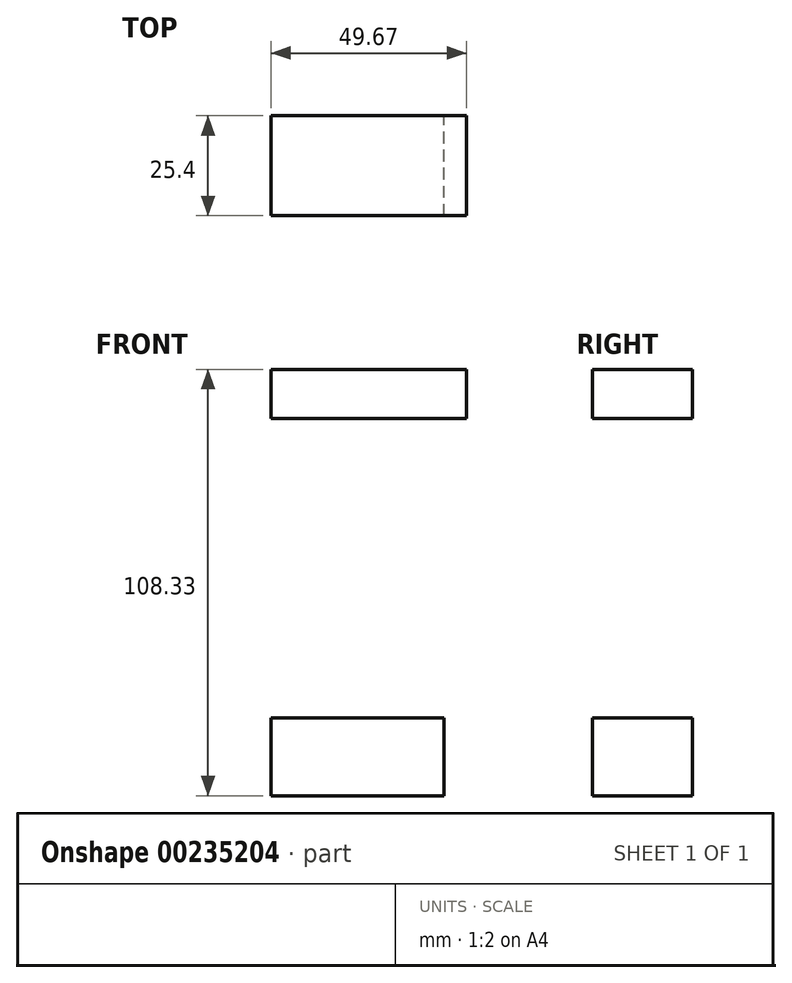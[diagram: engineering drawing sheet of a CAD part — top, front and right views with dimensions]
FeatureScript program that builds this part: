
annotation { "Feature Type Name" : "Feature", "Feature Type Description" : "" }
export const myFeature = defineFeature(function(context is Context, id is Id, definition is map)
    precondition{}
    {
        {
            var Q0;
            Q0=qCreatedBy(makeId("Front.planeOp"),FACE);
            var sketch = newSketch(context, id + "F0", { "sketchPlane" : qUnion([Q0])});
            skLineSegment(sketch, "E0.bottom", {"start": v(49.67, 35.29) * mm, "end": v(0, 35.29) * mm});
            skLineSegment(sketch, "E0.top", {"start": v(49.67, 47.75) * mm, "end": v(0, 47.75) * mm});
            skLineSegment(sketch, "E0.left", {"start": v(49.67, 35.29) * mm, "end": v(49.67, 47.75) * mm});
            skLineSegment(sketch, "E0.right", {"start": v(0, 35.29) * mm, "end": v(0, 47.75) * mm});
            skLineSegment(sketch, "E1.bottom", {"start": v(0, 35.29) * mm, "end": v(21.45, 35.29) * mm});
            skLineSegment(sketch, "E1.top", {"start": v(0, -40.78) * mm, "end": v(21.45, -40.78) * mm});
            skLineSegment(sketch, "E1.left", {"start": v(0, 35.29) * mm, "end": v(0, -40.78) * mm});
            skLineSegment(sketch, "E1.right", {"start": v(21.45, 35.29) * mm, "end": v(21.45, -40.78) * mm});
            skLineSegment(sketch, "E2.bottom", {"start": v(0, -40.78) * mm, "end": v(44, -40.78) * mm});
            skLineSegment(sketch, "E2.top", {"start": v(0, -60.58) * mm, "end": v(44, -60.58) * mm});
            skLineSegment(sketch, "E2.left", {"start": v(0, -40.78) * mm, "end": v(0, -60.58) * mm});
            skLineSegment(sketch, "E2.right", {"start": v(44, -40.78) * mm, "end": v(44, -60.58) * mm});
            skSolve(sketch);
        }
        {
            var Q0;
            Q0=makeQuery(id+"F0.imprint","IMPRINT",FACE,{"disambiguationData":[TD([[makeQuery(id+"F0.imprint","IMPRINT",EDGE,{"derivedFrom":sQuery(id+"F0.wireOp",EDGE,"E0.bottom")}),-1.0]])]});
            var Q1;
            Q1=makeQuery(id+"F0.imprint","IMPRINT",FACE,{"disambiguationData":[TD([[makeQuery(id+"F0.imprint","IMPRINT",EDGE,{"derivedFrom":sQuery(id+"F0.wireOp",EDGE,"E1.bottom")}),-1.0]])]});
            var Q2;
            Q2=makeQuery(id+"F0.imprint","IMPRINT",FACE,{"disambiguationData":[TD([[makeQuery(id+"F0.imprint","IMPRINT",EDGE,{"derivedFrom":sQuery(id+"F0.wireOp",EDGE,"E2.top")}),1.0]])]});
            extrude(context, id + "F1", {"entities" : qUnion([Q0, Q1, Q2]), "endBound" : BoundingType.SYMMETRIC, "depth" : 25.4 * mm});
        }
    });
